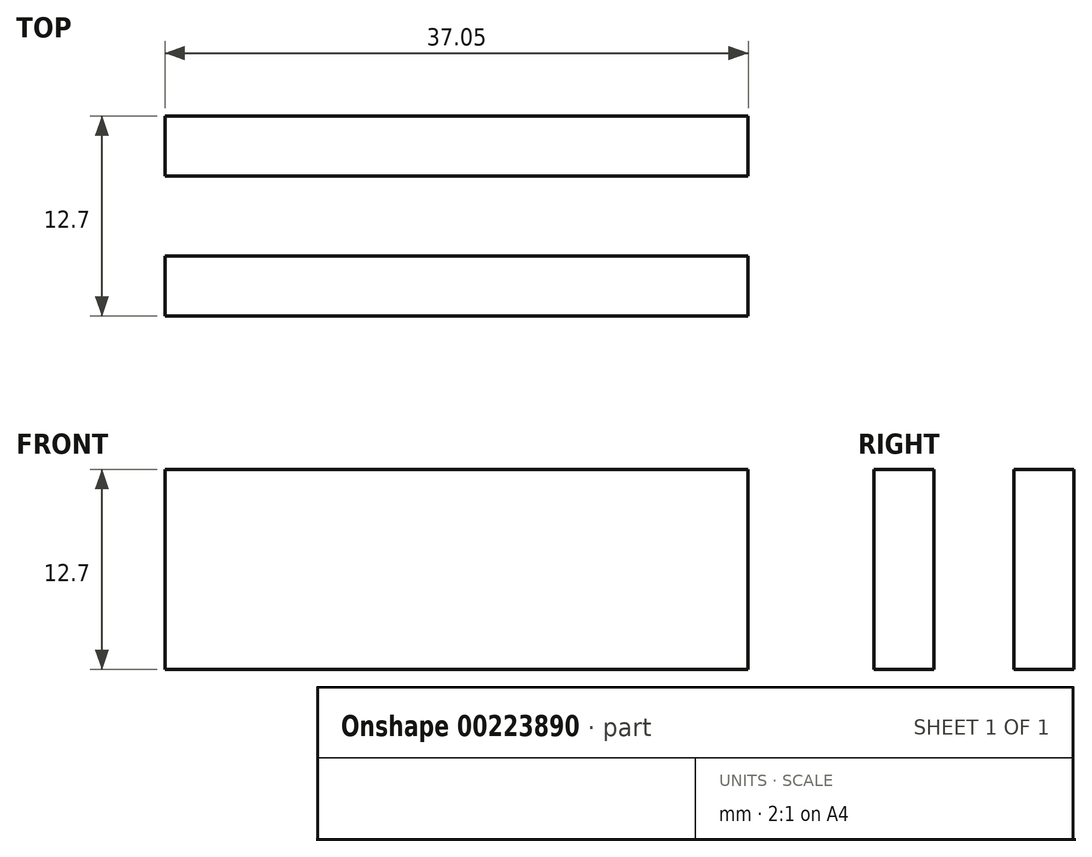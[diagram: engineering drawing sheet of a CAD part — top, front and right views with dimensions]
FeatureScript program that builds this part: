
annotation { "Feature Type Name" : "Feature", "Feature Type Description" : "" }
export const myFeature = defineFeature(function(context is Context, id is Id, definition is map)
    precondition{}
    {
        {
            var Q0;
            Q0=qCreatedBy(makeId("Top.planeOp"),FACE);
            var sketch = newSketch(context, id + "F0", { "sketchPlane" : qUnion([Q0])});
            skLineSegment(sketch, "E0", {"start": v(-56.16, 25.02) * mm, "end": v(-19.11, 25.02) * mm});
            skLineSegment(sketch, "E1", {"start": v(-19.11, 25.02) * mm, "end": v(-19.11, 12.32) * mm});
            skLineSegment(sketch, "E2", {"start": v(-19.11, 12.32) * mm, "end": v(-56.16, 12.32) * mm});
            skLineSegment(sketch, "E3", {"start": v(-56.16, 12.32) * mm, "end": v(-56.16, 25.02) * mm});
            skSolve(sketch);
        }
        {
            var Q0;
            Q0=makeQuery(id+"F0.imprint","IMPRINT",FACE,{"disambiguationData":[TD([[makeQuery(id+"F0.imprint","IMPRINT",EDGE,{"derivedFrom":sQuery(id+"F0.wireOp",EDGE,"E0")}),-1.0]])]});
            extrude(context, id + "F1", {"entities" : qUnion([Q0]), "depth" : 12.7 * mm});
        }
        {
            var Q0;
            Q0=makeQuery(id+"F1.opExtrude","CAP_FACE",FACE,{"disambiguationData":[OSD([sQuery(id+"F0.wireOp",EDGE,"E0"),sQuery(id+"F0.wireOp",EDGE,"E1"),sQuery(id+"F0.wireOp",EDGE,"E2"),sQuery(id+"F0.wireOp",EDGE,"E3")])],"isStart":false});
            var sketch = newSketch(context, id + "F2", { "sketchPlane" : qUnion([Q0])});
            skLineSegment(sketch, "E4", {"start": v(-19.11, 21.2) * mm, "end": v(-19.11, 16.13) * mm});
            skLineSegment(sketch, "E5", {"start": v(-19.11, 16.13) * mm, "end": v(-57.21, 16.13) * mm});
            skLineSegment(sketch, "E6", {"start": v(-57.21, 16.13) * mm, "end": v(-57.21, 21.2) * mm});
            skLineSegment(sketch, "E7", {"start": v(-57.21, 21.2) * mm, "end": v(-19.11, 21.2) * mm});
            skPoint(sketch, "E8.startSnap0", {"position": v(-37.64, 25.02) * mm});
            skSolve(sketch);
        }
        {
            var Q0;
            Q0 = qSketchRegion(id + "F2", true);
            extrude(context, id + "F3", {"entities" : qUnion([Q0]), "operationType" : NewBodyOperationType.REMOVE, "oppositeDirection" : true, "depth" : 25.4 * mm});
        }
    });
